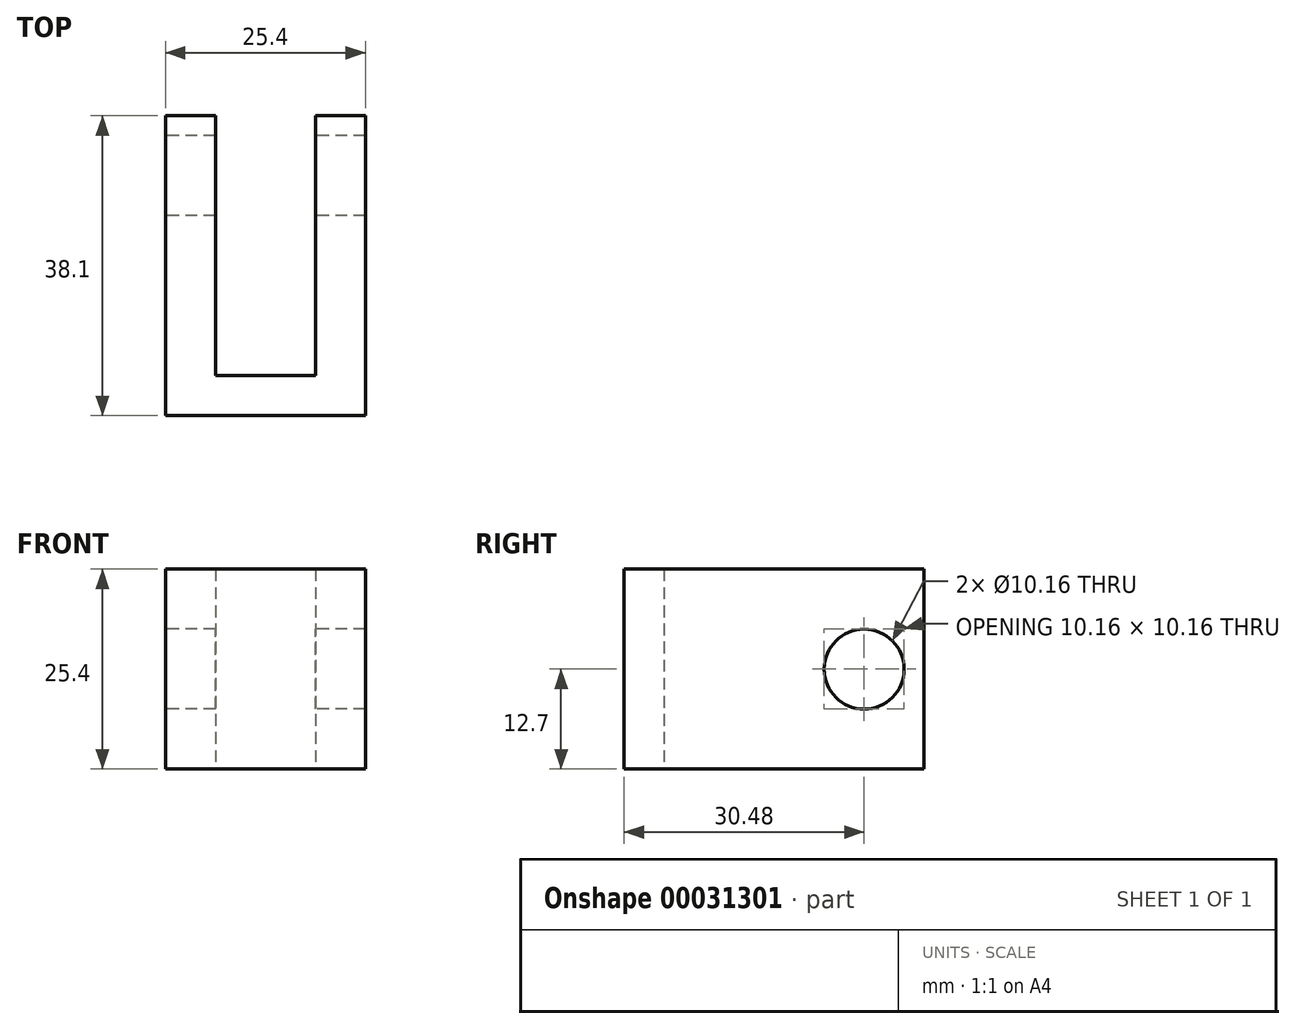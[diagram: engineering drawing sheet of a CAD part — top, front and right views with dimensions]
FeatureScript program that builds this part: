
annotation { "Feature Type Name" : "Feature", "Feature Type Description" : "" }
export const myFeature = defineFeature(function(context is Context, id is Id, definition is map)
    precondition{}
    {
        {
            var Q0;
            Q0=qCreatedBy(makeId("Top.planeOp"),FACE);
            var sketch = newSketch(context, id + "F0", { "sketchPlane" : qUnion([Q0])});
            skLineSegment(sketch, "E0.bottom", {"start": v(-25.4, 38.1) * mm, "end": v(-19.05, 38.1) * mm});
            skLineSegment(sketch, "E0.top", {"start": v(-25.4, 0) * mm, "end": v(0, 0) * mm});
            skLineSegment(sketch, "E0.left", {"start": v(-25.4, 38.1) * mm, "end": v(-25.4, 0) * mm});
            skLineSegment(sketch, "E0.right", {"start": v(0, 38.1) * mm, "end": v(0, 0) * mm});
            skLineSegment(sketch, "E1.top", {"start": v(-19.05, 5.08) * mm, "end": v(-6.35, 5.08) * mm});
            skLineSegment(sketch, "E1.left", {"start": v(-19.05, 38.1) * mm, "end": v(-19.05, 5.08) * mm});
            skLineSegment(sketch, "E1.right", {"start": v(-6.35, 38.1) * mm, "end": v(-6.35, 5.08) * mm});
            skLineSegment(sketch, "E2.trimOffspring", {"start": v(-6.35, 38.1) * mm, "end": v(0, 38.1) * mm});
            skSolve(sketch);
        }
        {
            var Q0;
            Q0=makeQuery(id+"F0.imprint","IMPRINT",FACE,{"disambiguationData":[TD([[makeQuery(id+"F0.imprint","IMPRINT",EDGE,{"derivedFrom":sQuery(id+"F0.wireOp",EDGE,"E0.bottom")}),-1.0]])]});
            extrude(context, id + "F1", {"entities" : qUnion([Q0]), "depth" : 25.4 * mm});
        }
        {
            var Q0;
            Q0=makeQuery(id+"F1.opExtrude","SWEPT_FACE",FACE,{"disambiguationData":[OSD([sQuery(id+"F0.wireOp",EDGE,"E0.left")])]});
            var sketch = newSketch(context, id + "F2", { "sketchPlane" : qUnion([Q0])});
            skCircle(sketch, "E3", {"center": v(-30.48, 12.7) * mm, "radius": 5.08 * mm});
            skSolve(sketch);
        }
        {
            var Q0;
            Q0=makeQuery(id+"F2.imprint","IMPRINT",FACE,{"disambiguationData":[TD([[makeQuery(id+"F2.imprint","IMPRINT",EDGE,{"derivedFrom":sQuery(id+"F2.wireOp",EDGE,"E3")}),1.0]])]});
            extrude(context, id + "F3", {"entities" : qUnion([Q0]), "operationType" : NewBodyOperationType.REMOVE, "oppositeDirection" : true, "depth" : 25.4 * mm});
        }
    });
